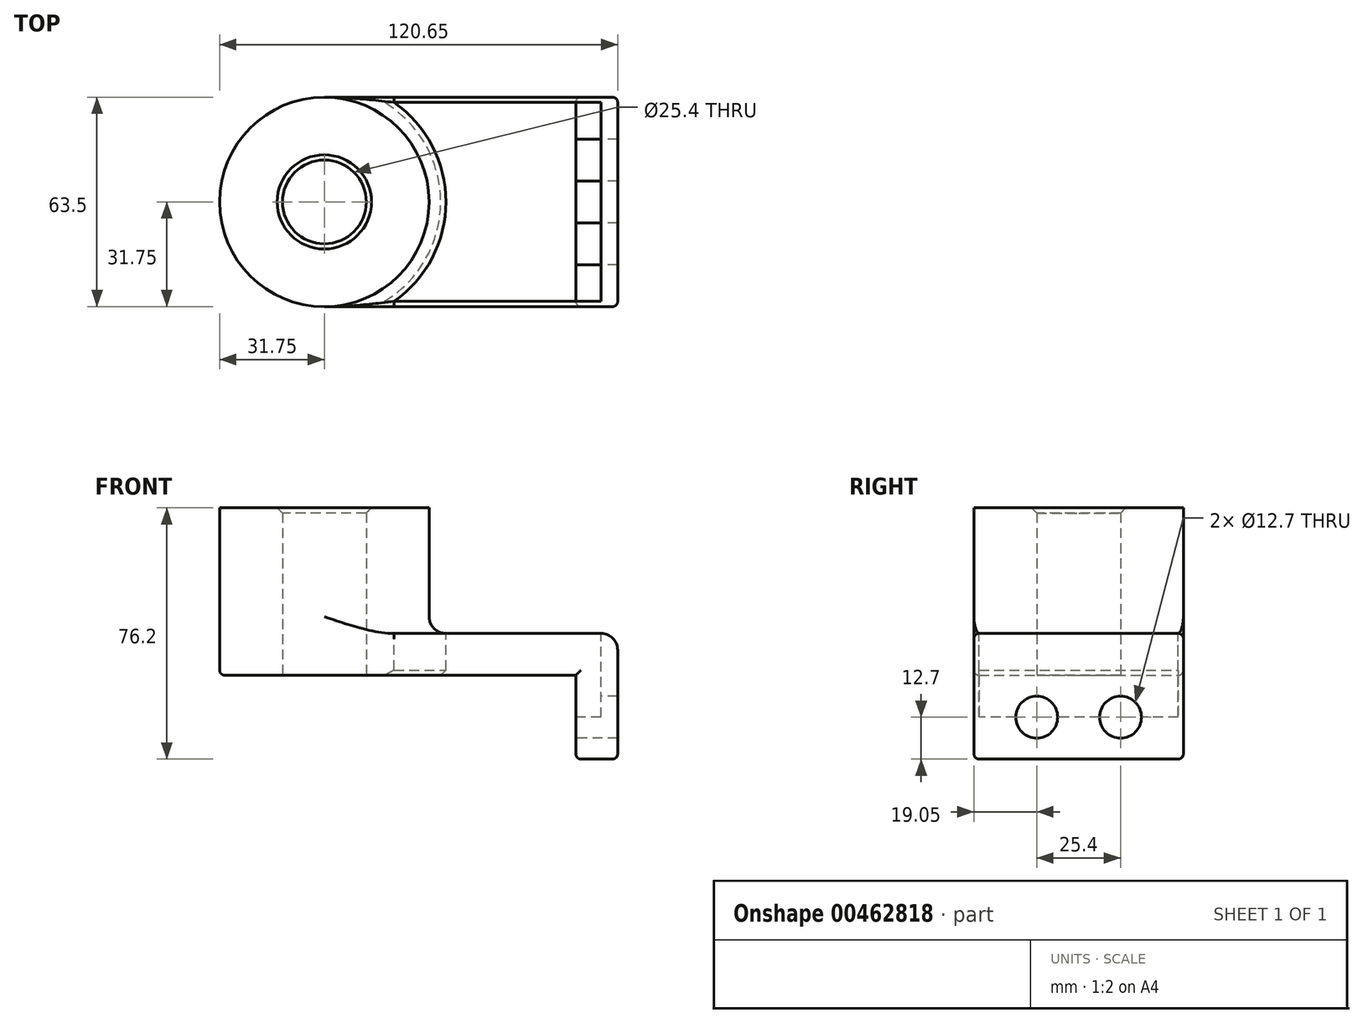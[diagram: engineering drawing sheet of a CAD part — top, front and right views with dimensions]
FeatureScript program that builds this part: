
annotation { "Feature Type Name" : "Feature", "Feature Type Description" : "" }
export const myFeature = defineFeature(function(context is Context, id is Id, definition is map)
    precondition{}
    {
        {
            var Q0;
            Q0=qCreatedBy(makeId("Top.planeOp"),FACE);
            var sketch = newSketch(context, id + "F0", { "sketchPlane" : qUnion([Q0])});
            skLineSegment(sketch, "E0.bottom", {"start": v(38.1, -31.75) * mm, "end": v(-38.1, -31.75) * mm});
            skLineSegment(sketch, "E0.top", {"start": v(38.1, 31.75) * mm, "end": v(-38.1, 31.75) * mm});
            skLineSegment(sketch, "E0.left", {"start": v(38.1, -31.75) * mm, "end": v(38.1, 31.75) * mm});
            skLineSegment(sketch, "E0.right", {"start": v(-38.1, -31.75) * mm, "end": v(-38.1, 31.75) * mm});
            skPoint(sketch, "E0.middle", {"position": v(0, 0) * mm});
            skCircle(sketch, "E1", {"center": v(-38.1, 0) * mm, "radius": 31.75 * mm});
            skCircle(sketch, "E2", {"center": v(-38.1, 0) * mm, "radius": 12.7 * mm});
            skSolve(sketch);
        }
        {
            var Q0;
            {var subQ1=sQuery(id+"F0.wireOp",EDGE,"E0.bottom");Q0=makeQuery(id+"F0.imprint","IMPRINT",FACE,{"disambiguationData":[TD([[makeQuery(id+"F0.imprint","IMPRINT",EDGE,{"derivedFrom":subQ1}),-1.0]])]});}
            var Q1;
            {var subQ0=sQuery(id+"F0.wireOp",EDGE,"E1");var subQ1=sQuery(id+"F0.wireOp",EDGE,"E0.right");var subQ2=makeQuery(id+"F0.imprint","INTERSECT",VERTEX,{"disambiguationData":[OD(0.0)],"derivedFrom":[subQ1,subQ0]});Q1=makeQuery(id+"F0.imprint","IMPRINT",FACE,{"disambiguationData":[TD([[makeQuery(id+"F0.imprint","IMPRINT",EDGE,{"disambiguationData":[TD([[subQ2,-1.0]])],"derivedFrom":subQ1}),1.0]])]});}
            var Q2;
            {var subQ0=sQuery(id+"F0.wireOp",EDGE,"E2");var subQ1=sQuery(id+"F0.wireOp",EDGE,"E0.right");var subQ2=makeQuery(id+"F0.imprint","INTERSECT",VERTEX,{"disambiguationData":[OD(0.0)],"derivedFrom":[subQ1,subQ0]});Q2=makeQuery(id+"F0.imprint","IMPRINT",FACE,{"disambiguationData":[TD([[makeQuery(id+"F0.imprint","IMPRINT",EDGE,{"disambiguationData":[TD([[subQ2,-1.0]])],"derivedFrom":subQ1}),1.0]])]});}
            var Q3;
            {var subQ0=sQuery(id+"F0.wireOp",EDGE,"E2");var subQ1=sQuery(id+"F0.wireOp",EDGE,"E0.right");var subQ2=makeQuery(id+"F0.imprint","INTERSECT",VERTEX,{"disambiguationData":[OD(0.0)],"derivedFrom":[subQ1,subQ0]});Q3=makeQuery(id+"F0.imprint","IMPRINT",FACE,{"disambiguationData":[TD([[makeQuery(id+"F0.imprint","IMPRINT",EDGE,{"disambiguationData":[TD([[subQ2,-1.0]])],"derivedFrom":subQ1}),-1.0]])]});}
            var Q4;
            {var subQ0=sQuery(id+"F0.wireOp",EDGE,"E1");var subQ1=sQuery(id+"F0.wireOp",EDGE,"E0.right");var subQ2=makeQuery(id+"F0.imprint","INTERSECT",VERTEX,{"disambiguationData":[OD(0.0)],"derivedFrom":[subQ1,subQ0]});Q4=makeQuery(id+"F0.imprint","IMPRINT",FACE,{"disambiguationData":[TD([[makeQuery(id+"F0.imprint","IMPRINT",EDGE,{"disambiguationData":[TD([[subQ2,-1.0]])],"derivedFrom":subQ1}),-1.0]])]});}
            extrude(context, id + "F1", {"entities" : qUnion([Q0, Q1, Q2, Q3, Q4]), "depth" : 12.7 * mm});
        }
        {
            var Q0;
            {var subQ0=sQuery(id+"F0.wireOp",EDGE,"E1");var subQ1=sQuery(id+"F0.wireOp",EDGE,"E0.right");var subQ2=makeQuery(id+"F0.imprint","INTERSECT",VERTEX,{"disambiguationData":[OD(0.0)],"derivedFrom":[subQ1,subQ0]});Q0=makeQuery(id+"F0.imprint","IMPRINT",FACE,{"disambiguationData":[TD([[makeQuery(id+"F0.imprint","IMPRINT",EDGE,{"disambiguationData":[TD([[subQ2,-1.0]])],"derivedFrom":subQ1}),-1.0]])]});}
            var Q1;
            {var subQ0=sQuery(id+"F0.wireOp",EDGE,"E1");var subQ1=sQuery(id+"F0.wireOp",EDGE,"E0.right");var subQ2=makeQuery(id+"F0.imprint","INTERSECT",VERTEX,{"disambiguationData":[OD(0.0)],"derivedFrom":[subQ1,subQ0]});Q1=makeQuery(id+"F0.imprint","IMPRINT",FACE,{"disambiguationData":[TD([[makeQuery(id+"F0.imprint","IMPRINT",EDGE,{"disambiguationData":[TD([[subQ2,-1.0]])],"derivedFrom":subQ1}),1.0]])]});}
            extrude(context, id + "F2", {"entities" : qUnion([Q0, Q1]), "operationType" : NewBodyOperationType.ADD, "depth" : 50.8 * mm});
        }
        {
            var Q0;
            Q0=makeQuery(id+"F1.opExtrude","SWEPT_FACE",FACE,{"disambiguationData":[OSD([sQuery(id+"F0.wireOp",EDGE,"E0.left")])]});
            var sketch = newSketch(context, id + "F3", { "sketchPlane" : qUnion([Q0])});
            skLineSegment(sketch, "E3.bottom", {"start": v(-31.75, 12.7) * mm, "end": v(31.75, 12.7) * mm});
            skLineSegment(sketch, "E3.top", {"start": v(-31.75, -25.4) * mm, "end": v(31.75, -25.4) * mm});
            skLineSegment(sketch, "E3.left", {"start": v(-31.75, 12.7) * mm, "end": v(-31.75, -25.4) * mm});
            skLineSegment(sketch, "E3.right", {"start": v(31.75, 12.7) * mm, "end": v(31.75, -25.4) * mm});
            skCircle(sketch, "E4", {"center": v(-12.7, -12.7) * mm, "radius": 6.35 * mm});
            skLineSegment(sketch, "E5", {"start": v(0, 0) * mm, "end": v(0, -25.4) * mm});
            skCircle(sketch, "E6.MirrorC", {"center": v(12.7, -12.7) * mm, "radius": 6.35 * mm});
            skSolve(sketch);
        }
        {
            var Q0;
            Q0 = qSketchRegion(id + "F3", true);
            extrude(context, id + "F4", {"entities" : qUnion([Q0]), "operationType" : NewBodyOperationType.ADD, "depth" : 12.7 * mm});
        }
        {
            var Q0;
            {var subQ0=sQuery(id+"F0.wireOp",EDGE,"E1");Q0=makeQuery(id+"F2.boolean.opBoolean","INTERSECT",EDGE,{"derivedFrom":[makeQuery(id+"F1.opExtrude","CAP_FACE",FACE,{"disambiguationData":[OSD([sQuery(id+"F0.wireOp",EDGE,"E0.bottom"),sQuery(id+"F0.wireOp",EDGE,"E0.top"),sQuery(id+"F0.wireOp",EDGE,"E0.left"),sQuery(id+"F0.wireOp",EDGE,"E0.right"),subQ0])],"isStart":false}),makeQuery(id+"F2.opExtrude","SWEPT_FACE",FACE,{"disambiguationData":[OSD([subQ0])]})]});}
            fillet(context, id + "F5", {"entities" : qUnion([Q0]), "radius" : 5.08 * mm, "tangentPropagation" : true, "allowEdgeOverflow" : false});
        }
        {
            var Q0;
            Q0=makeQuery(id+"F4.opExtrude","CAP_EDGE",EDGE,{"disambiguationData":[OSD([sQuery(id+"F3.wireOp",EDGE,"E3.bottom")])],"isStart":false});
            fillet(context, id + "F6", {"entities" : qUnion([Q0]), "radius" : 5.08 * mm, "tangentPropagation" : true, "allowEdgeOverflow" : false});
        }
        {
            var Q0;
            Q0=makeQuery(id+"F4.boolean.opBoolean","MERGE",EDGE,{"derivedFrom":[makeQuery(id+"F1.opExtrude","CAP_EDGE",EDGE,{"disambiguationData":[OSD([sQuery(id+"F0.wireOp",EDGE,"E0.bottom")])],"isStart":false}),makeQuery(id+"F4.opExtrude","SWEPT_EDGE",EDGE,{"disambiguationData":[OSD([sQuery(id+"F3.wireOp",EDGE,"E3.bottom"),sQuery(id+"F3.wireOp",EDGE,"E3.left")])]})]});
            var Q1;
            Q1=makeQuery(id+"F4.opExtrude","CAP_EDGE",EDGE,{"disambiguationData":[OSD([sQuery(id+"F3.wireOp",EDGE,"E3.right")])],"isStart":false});
            fillet(context, id + "F7", {"entities" : qUnion([Q0, Q1]), "radius" : 1.59 * mm, "tangentPropagation" : true, "allowEdgeOverflow" : false});
        }
        {
            var Q0;
            Q0=makeQuery(id+"F1.opExtrude","CAP_EDGE",EDGE,{"disambiguationData":[OSD([sQuery(id+"F0.wireOp",EDGE,"E0.bottom")])],"isStart":true});
            var Q1;
            Q1=makeQuery(id+"F4.opExtrude","CAP_EDGE",EDGE,{"disambiguationData":[OSD([sQuery(id+"F3.wireOp",EDGE,"E3.left")])],"isStart":true});
            var Q2;
            Q2=makeQuery(id+"F4.opExtrude","CAP_EDGE",EDGE,{"disambiguationData":[OSD([sQuery(id+"F3.wireOp",EDGE,"E3.top")])],"isStart":true});
            var Q3;
            Q3=makeQuery(id+"F4.opExtrude","CAP_EDGE",EDGE,{"disambiguationData":[OSD([sQuery(id+"F3.wireOp",EDGE,"E3.right")])],"isStart":true});
            var Q4;
            Q4=makeQuery(id+"F4.opExtrude","SWEPT_EDGE",EDGE,{"disambiguationData":[OSD([sQuery(id+"F3.wireOp",EDGE,"E3.top"),sQuery(id+"F3.wireOp",EDGE,"E3.right")])]});
            fillet(context, id + "F8", {"entities" : qUnion([Q0, Q1, Q2, Q3, Q4]), "radius" : 1.59 * mm, "tangentPropagation" : true, "allowEdgeOverflow" : false});
        }
        {
            var Q0;
            Q0=makeQuery(id+"F2.boolean.opBoolean","SPLIT",FACE,{"disambiguationData":[TD([makeQuery(id+"F2.opExtrude","SWEPT_FACE",FACE,{"disambiguationData":[OSD([sQuery(id+"F0.wireOp",EDGE,"E2")])]})])],"derivedFrom":makeQuery(id+"F1.opExtrude","CAP_FACE",FACE,{"disambiguationData":[OSD([sQuery(id+"F0.wireOp",EDGE,"E0.bottom"),sQuery(id+"F0.wireOp",EDGE,"E0.top"),sQuery(id+"F0.wireOp",EDGE,"E0.left"),sQuery(id+"F0.wireOp",EDGE,"E1")])],"isStart":false})});
            extrude(context, id + "F9", {"entities" : qUnion([Q0]), "operationType" : NewBodyOperationType.REMOVE, "oppositeDirection" : true, "depth" : 25.4 * mm});
        }
        {
            var Q0;
            Q0=makeQuery(id+"F2.opExtrude","CAP_EDGE",EDGE,{"disambiguationData":[OSD([sQuery(id+"F0.wireOp",EDGE,"E2")])],"isStart":false});
            var Q1;
            {var subQ0=sQuery(id+"F0.wireOp",EDGE,"E1");var subQ1=sQuery(id+"F0.wireOp",EDGE,"E0.left");var subQ2=sQuery(id+"F0.wireOp",EDGE,"E0.top");var subQ3=sQuery(id+"F0.wireOp",EDGE,"E0.bottom");Q1=makeQuery(id+"F9.boolean.opBoolean","INTERSECT",EDGE,{"derivedFrom":[makeQuery(id+"F1.opExtrude","CAP_FACE",FACE,{"disambiguationData":[OSD([subQ3,subQ2,subQ1,subQ0])],"isStart":true}),makeQuery(id+"F9.opExtrude","SWEPT_FACE",FACE,{"disambiguationData":[OSD([subQ3,subQ2,subQ1,subQ0,sQuery(id+"F0.wireOp",EDGE,"E2")])]})]});}
            chamfer(context, id + "F10", {"entities" : qUnion([Q0, Q1]), "width" : 1.59 * mm, "tangentPropagation" : true});
        }
    });
